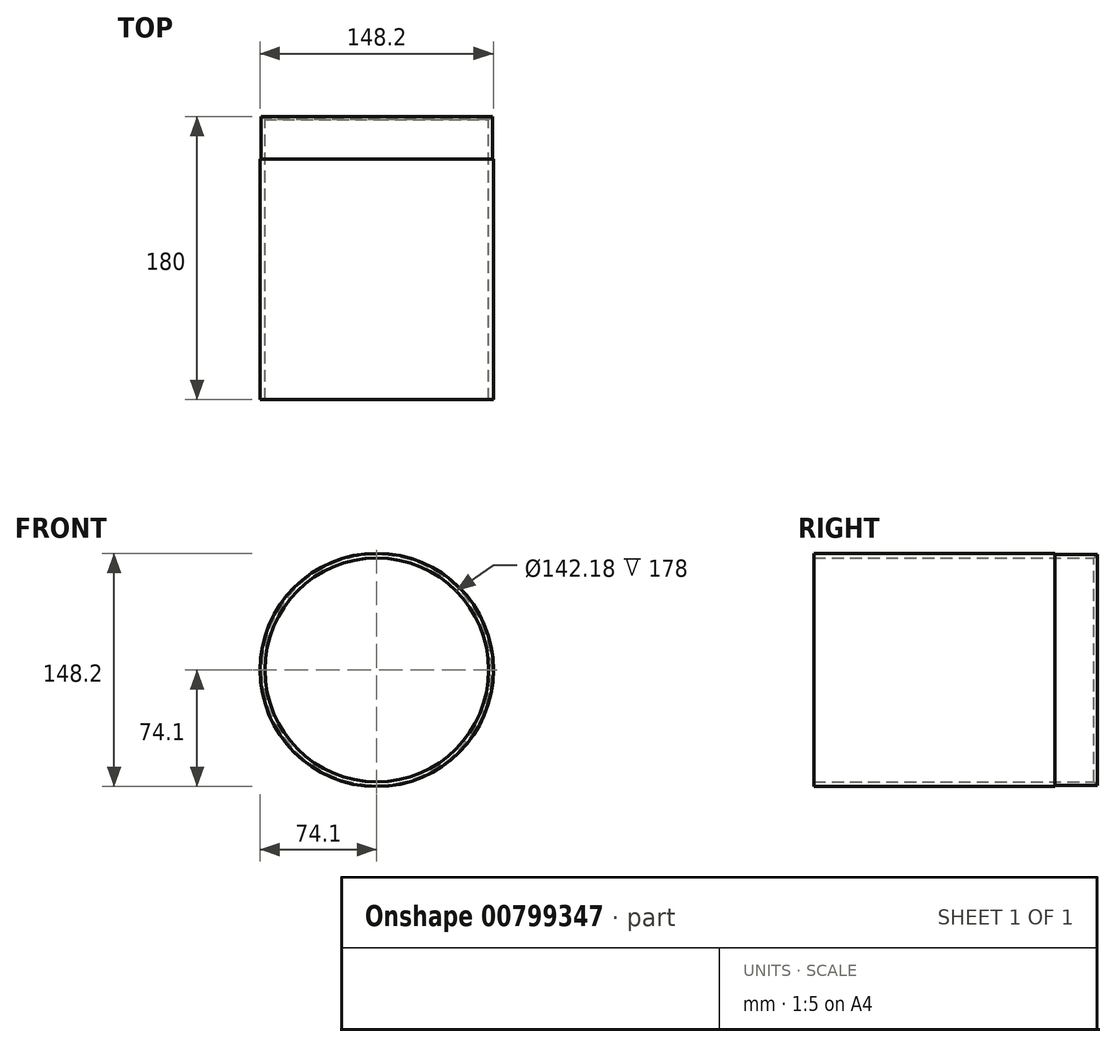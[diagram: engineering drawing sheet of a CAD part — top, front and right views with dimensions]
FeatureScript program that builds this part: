
annotation { "Feature Type Name" : "Feature", "Feature Type Description" : "" }
export const myFeature = defineFeature(function(context is Context, id is Id, definition is map)
    precondition{}
    {
        {
            var Q0;
            Q0=qCreatedBy(makeId("Front.planeOp"),FACE);
            var sketch = newSketch(context, id + "F0", { "sketchPlane" : qUnion([Q0])});
            skCircle(sketch, "E0", {"center": v(0, 0) * mm, "radius": 71.1 * mm});
            skCircle(sketch, "E1", {"center": v(0, 0) * mm, "radius": 74.1 * mm});
            skSolve(sketch);
        }
        {
            var Q0;
            Q0=makeQuery(id+"F0.imprint","IMPRINT",FACE,{"disambiguationData":[TD([[makeQuery(id+"F0.imprint","IMPRINT",EDGE,{"derivedFrom":sQuery(id+"F0.wireOp",EDGE,"E0")}),-1.0]])]});
            extrude(context, id + "F1", {"entities" : qUnion([Q0]), "depth" : 260 * mm, "offsetDistance" : 25 * mm});
        }
        {
            var Q0;
            Q0=qCreatedBy(makeId("Front.planeOp"),FACE);
            var sketch = newSketch(context, id + "F2", { "sketchPlane" : qUnion([Q0])});
            skCircle(sketch, "E2", {"center": v(0, 0) * mm, "radius": 73.4 * mm});
            skCircle(sketch, "E3", {"center": v(0, 0) * mm, "radius": 78.65 * mm});
            skSolve(sketch);
        }
        {
            var Q0;
            Q0=makeQuery(id+"F2.imprint","IMPRINT",FACE,{"disambiguationData":[TD([[makeQuery(id+"F2.imprint","IMPRINT",EDGE,{"derivedFrom":sQuery(id+"F2.wireOp",EDGE,"E2")}),-1.0]])]});
            extrude(context, id + "F3", {"entities" : qUnion([Q0]), "operationType" : NewBodyOperationType.REMOVE, "offsetDistance" : 25 * mm, "depth" : 27 * mm});
        }
        {
            var Q0;
            Q0=makeQuery(id+"F1.opExtrude","CAP_FACE",FACE,{"disambiguationData":[OSD([sQuery(id+"F0.wireOp",EDGE,"E0"),sQuery(id+"F0.wireOp",EDGE,"E1")])],"isStart":false});
            var sketch = newSketch(context, id + "F4", { "sketchPlane" : qUnion([Q0])});
            skCircle(sketch, "E4", {"center": v(0, 0) * mm, "radius": 73.4 * mm});
            skSolve(sketch);
        }
        {
            var Q0;
            Q0=makeQuery(id+"F4.imprint","IMPRINT",FACE,{"disambiguationData":[TD([[makeQuery(id+"F4.imprint","IMPRINT",EDGE,{"derivedFrom":sQuery(id+"F4.wireOp",EDGE,"E4")}),-1.0]])]});
            extrude(context, id + "F5", {"entities" : qUnion([Q0]), "operationType" : NewBodyOperationType.REMOVE, "oppositeDirection" : true, "depth" : 27 * mm, "offsetDistance" : 25 * mm});
        }
        {
            var Q0;
            Q0=makeQuery(id+"F1.opExtrude","CAP_EDGE",EDGE,{"disambiguationData":[OSD([sQuery(id+"F0.wireOp",EDGE,"E0")])],"isStart":false});
            var Q1;
            Q1=makeQuery(id+"F1.opExtrude","CAP_EDGE",EDGE,{"disambiguationData":[OSD([sQuery(id+"F0.wireOp",EDGE,"E0")])],"isStart":true});
            chamfer(context, id + "F6", {"entities" : qUnion([Q0, Q1]), "width" : 2 * mm, "tangentPropagation" : true});
        }
        {
            var Q0;
            Q0=makeQuery(id+"F1.opExtrude","CAP_FACE",FACE,{"disambiguationData":[OSD([sQuery(id+"F0.wireOp",EDGE,"E0"),sQuery(id+"F0.wireOp",EDGE,"E1")])],"isStart":false});
            var sketch = newSketch(context, id + "F7", { "sketchPlane" : qUnion([Q0])});
            skCircle(sketch, "E5", {"center": v(0, 0) * mm, "radius": 95.05 * mm});
            skCircle(sketch, "E6", {"center": v(0, 0) * mm, "radius": 7.41 * mm});
            skSolve(sketch);
        }
        {
            var Q0;
            Q0 = qSketchRegion(id + "F7", true);
            extrude(context, id + "F8", {"entities" : qUnion([Q0]), "operationType" : NewBodyOperationType.REMOVE, "oppositeDirection" : true, "depth" : 80 * mm, "offsetDistance" : 25 * mm});
        }
    });
